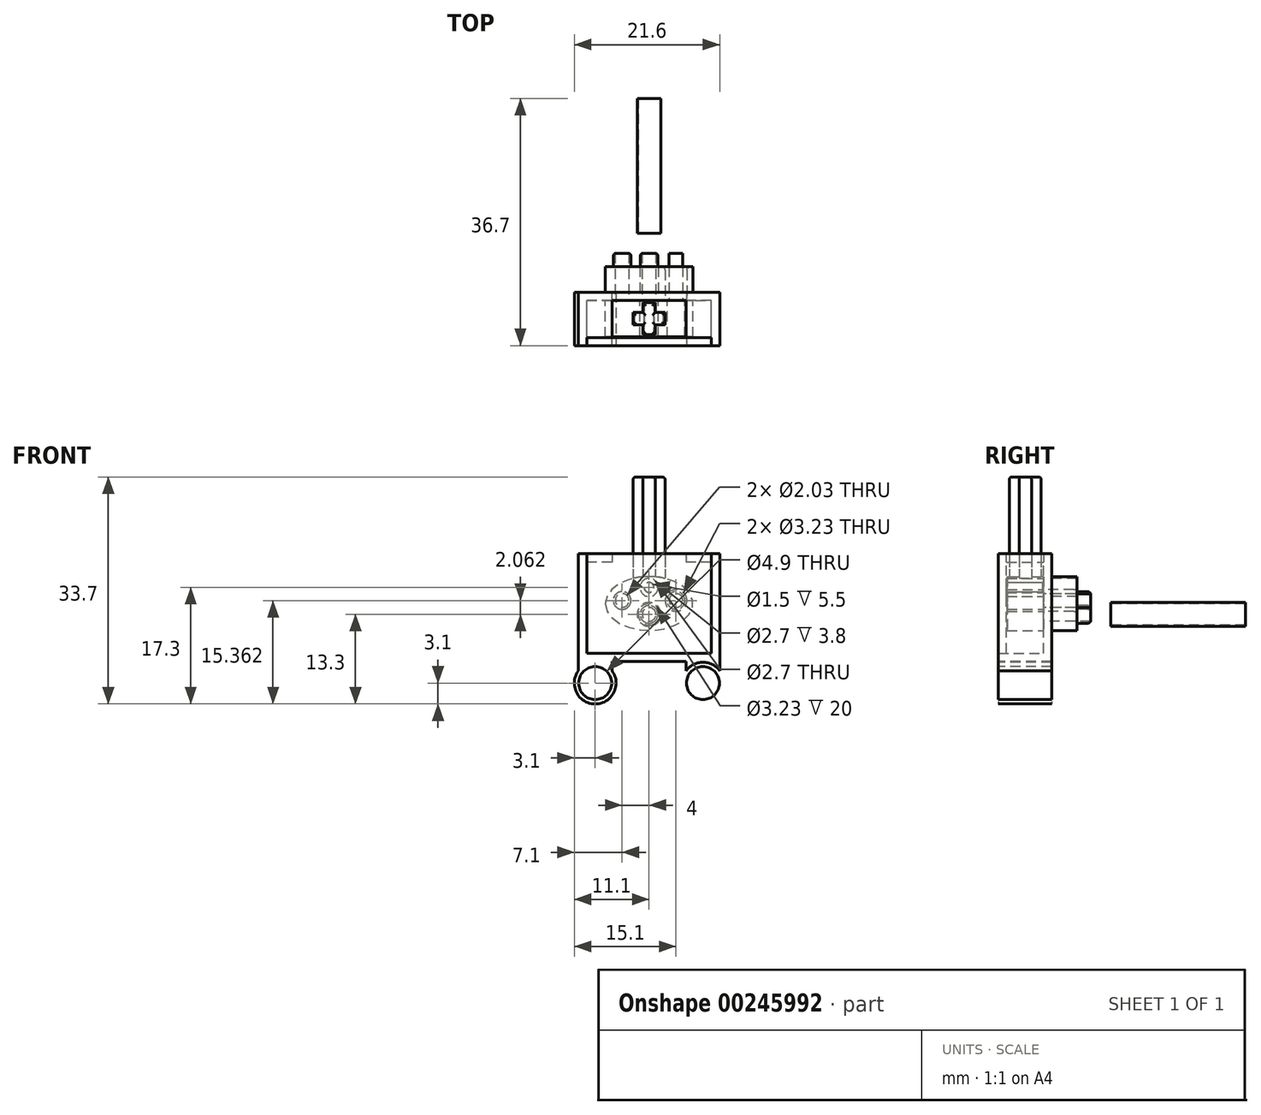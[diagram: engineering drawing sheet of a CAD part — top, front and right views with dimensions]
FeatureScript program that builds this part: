
annotation { "Feature Type Name" : "Feature", "Feature Type Description" : "" }
export const myFeature = defineFeature(function(context is Context, id is Id, definition is map)
    precondition{}
    {
        {
            var Q0;
            Q0=qCreatedBy(makeId("Front.planeOp"),FACE);
            var sketch = newSketch(context, id + "F0", { "sketchPlane" : qUnion([Q0])});
            skLineSegment(sketch, "E0", {"start": v(0, 5) * mm, "end": v(-10.5, 5) * mm});
            skLineSegment(sketch, "E1", {"start": v(-10.5, 5) * mm, "end": v(-10.5, -11) * mm});
            skLineSegment(sketch, "E2", {"start": v(-10.5, -11) * mm, "end": v(10.5, -11) * mm});
            skLineSegment(sketch, "E3", {"start": v(10.5, -11) * mm, "end": v(10.5, 5) * mm});
            skLineSegment(sketch, "E4", {"start": v(10.5, 5) * mm, "end": v(0, 5) * mm});
            skLineSegment(sketch, "E5", {"start": v(0, 5) * mm, "end": v(0, 0) * mm, "construction": true});
            skLineSegment(sketch, "E6.0", {"start": v(-9.25, 3.75) * mm, "end": v(-9.25, -9.75) * mm});
            skLineSegment(sketch, "E6.1", {"start": v(0, 3.75) * mm, "end": v(-9.25, 3.75) * mm});
            skLineSegment(sketch, "E6.2", {"start": v(-9.25, -9.75) * mm, "end": v(9.25, -9.75) * mm});
            skLineSegment(sketch, "E6.3", {"start": v(9.25, -9.75) * mm, "end": v(9.25, 3.75) * mm});
            skLineSegment(sketch, "E6.4", {"start": v(9.25, 3.75) * mm, "end": v(0, 3.75) * mm});
            skLineSegment(sketch, "E7", {"start": v(-5.5, 5) * mm, "end": v(-5.5, 3.75) * mm});
            skLineSegment(sketch, "E8.MirrorCS", {"start": v(5.5, 5) * mm, "end": v(5.5, 3.75) * mm});
            skLineSegment(sketch, "E9", {"start": v(0, -14.2) * mm, "end": v(-8, -14.2) * mm, "construction": true});
            skCircle(sketch, "E10", {"center": v(-8, -14.2) * mm, "radius": 2.45 * mm});
            skCircle(sketch, "E11.0", {"center": v(-8, -14.2) * mm, "radius": 3.1 * mm});
            skLineSegment(sketch, "E12.MirrorCS", {"start": v(0, -14.2) * mm, "end": v(8, -14.2) * mm, "construction": true});
            skCircle(sketch, "E13.MirrorC", {"center": v(8, -14.2) * mm, "radius": 2.45 * mm});
            skCircle(sketch, "E14.MirrorC", {"center": v(8, -14.2) * mm, "radius": 3.1 * mm});
            skLineSegment(sketch, "E15", {"start": v(-10.5, -11) * mm, "end": v(-10.5, -12.37) * mm});
            skLineSegment(sketch, "E16", {"start": v(-5.5, -11) * mm, "end": v(-5.5, -12.37) * mm});
            skLineSegment(sketch, "E17.MirrorCS", {"start": v(10.5, -11) * mm, "end": v(10.5, -12.37) * mm});
            skLineSegment(sketch, "E18.MirrorCS", {"start": v(5.5, -11) * mm, "end": v(5.5, -12.37) * mm});
            skLineSegment(sketch, "E19", {"start": v(-9.25, 3.75) * mm, "end": v(-9.25, 5) * mm});
            skLineSegment(sketch, "E20", {"start": v(9.25, 3.75) * mm, "end": v(9.25, 5) * mm});
            skCircle(sketch, "E21", {"center": v(0, 0) * mm, "radius": 0.75 * mm});
            skCircle(sketch, "E22.0", {"center": v(0, 0) * mm, "radius": 1.35 * mm});
            skCircle(sketch, "E23", {"center": v(0, -4) * mm, "radius": 1.62 * mm});
            skCircle(sketch, "E24", {"center": v(-4, -1.94) * mm, "radius": 1.62 * mm});
            skCircle(sketch, "E25.0", {"center": v(-4, -1.94) * mm, "radius": 1.02 * mm});
            skCircle(sketch, "E26.0", {"center": v(0, -4) * mm, "radius": 1.02 * mm});
            skCircle(sketch, "E27.MirrorC", {"center": v(4, -1.94) * mm, "radius": 1.62 * mm});
            skCircle(sketch, "E28.MirrorC", {"center": v(4, -1.94) * mm, "radius": 1.02 * mm});
            skCircle(sketch, "E29.0", {"center": v(0, -4) * mm, "radius": 1.32 * mm});
            skCircle(sketch, "E30.0", {"center": v(-4, -1.94) * mm, "radius": 1.32 * mm});
            skCircle(sketch, "E31.MirrorC", {"center": v(4, -1.94) * mm, "radius": 1.32 * mm});
            skLineSegment(sketch, "E32", {"start": v(0, 0) * mm, "end": v(0, -14.2) * mm, "construction": true});
            skEllipse(sketch, "E33", {"center": v(0, -2.39) * mm, "majorRadius": 6.5 * mm, "minorRadius": 4 * mm, "majorAxis": v(-1, 0)});
            skSolve(sketch);
        }
        {
            var Q0;
            {var subQ1=sQuery(id+"F0.wireOp",EDGE,"E6.0");Q0=makeQuery(id+"F0.imprint","IMPRINT",FACE,{"disambiguationData":[TD([[makeQuery(id+"F0.imprint","IMPRINT",EDGE,{"derivedFrom":subQ1}),1.0]])]});}
            var Q1;
            {var subQ8=sQuery(id+"F0.wireOp",EDGE,"E1");Q1=makeQuery(id+"F0.imprint","IMPRINT",FACE,{"disambiguationData":[TD([[makeQuery(id+"F0.imprint","IMPRINT",EDGE,{"derivedFrom":subQ8}),1.0]])]});}
            var Q2;
            {var subQ7=sQuery(id+"F0.wireOp",EDGE,"E7");Q2=makeQuery(id+"F0.imprint","IMPRINT",FACE,{"disambiguationData":[TD([[makeQuery(id+"F0.imprint","IMPRINT",EDGE,{"derivedFrom":subQ7}),1.0]])]});}
            var Q3;
            Q3=makeQuery(id+"F0.imprint","IMPRINT",FACE,{"disambiguationData":[TD([[makeQuery(id+"F0.imprint","IMPRINT",EDGE,{"derivedFrom":sQuery(id+"F0.wireOp",EDGE,"E10")}),-1.0]])]});
            var Q4;
            {var subQ0=sQuery(id+"F0.wireOp",EDGE,"E15");Q4=makeQuery(id+"F0.imprint","IMPRINT",FACE,{"disambiguationData":[TD([[makeQuery(id+"F0.imprint","IMPRINT",EDGE,{"derivedFrom":subQ0}),1.0]])]});}
            var Q5;
            Q5=makeQuery(id+"F0.imprint","IMPRINT",FACE,{"disambiguationData":[TD([[makeQuery(id+"F0.imprint","IMPRINT",EDGE,{"derivedFrom":sQuery(id+"F0.wireOp",EDGE,"E13.MirrorC")}),1.0]])]});
            var Q6;
            {var subQ0=sQuery(id+"F0.wireOp",EDGE,"E17.MirrorCS");Q6=makeQuery(id+"F0.imprint","IMPRINT",FACE,{"disambiguationData":[TD([[makeQuery(id+"F0.imprint","IMPRINT",EDGE,{"derivedFrom":subQ0}),-1.0]])]});}
            var Q7;
            {var subQ0=sQuery(id+"F0.wireOp",EDGE,"E7");Q7=makeQuery(id+"F0.imprint","IMPRINT",FACE,{"disambiguationData":[TD([[makeQuery(id+"F0.imprint","IMPRINT",EDGE,{"derivedFrom":subQ0}),-1.0]])]});}
            var Q8;
            {var subQ0=sQuery(id+"F0.wireOp",EDGE,"E8.MirrorCS");Q8=makeQuery(id+"F0.imprint","IMPRINT",FACE,{"disambiguationData":[TD([[makeQuery(id+"F0.imprint","IMPRINT",EDGE,{"derivedFrom":subQ0}),1.0]])]});}
            var Q9;
            Q9=makeQuery(id+"F0.imprint","IMPRINT",FACE,{"disambiguationData":[TD([[makeQuery(id+"F0.imprint","IMPRINT",EDGE,{"derivedFrom":sQuery(id+"F0.wireOp",EDGE,"E21")}),1.0]])]});
            var Q10;
            Q10=makeQuery(id+"F0.imprint","IMPRINT",FACE,{"disambiguationData":[TD([[makeQuery(id+"F0.imprint","IMPRINT",EDGE,{"derivedFrom":sQuery(id+"F0.wireOp",EDGE,"E21")}),-1.0]])]});
            var Q11;
            Q11=makeQuery(id+"F0.imprint","IMPRINT",FACE,{"disambiguationData":[TD([[makeQuery(id+"F0.imprint","IMPRINT",EDGE,{"derivedFrom":sQuery(id+"F0.wireOp",EDGE,"E24")}),1.0]])]});
            var Q12;
            Q12=makeQuery(id+"F0.imprint","IMPRINT",FACE,{"disambiguationData":[TD([[makeQuery(id+"F0.imprint","IMPRINT",EDGE,{"derivedFrom":sQuery(id+"F0.wireOp",EDGE,"E23")}),1.0]])]});
            var Q13;
            Q13=makeQuery(id+"F0.imprint","IMPRINT",FACE,{"disambiguationData":[TD([[makeQuery(id+"F0.imprint","IMPRINT",EDGE,{"derivedFrom":sQuery(id+"F0.wireOp",EDGE,"E27.MirrorC")}),-1.0]])]});
            var Q14;
            Q14=makeQuery(id+"F0.imprint","IMPRINT",FACE,{"disambiguationData":[TD([[makeQuery(id+"F0.imprint","IMPRINT",EDGE,{"derivedFrom":sQuery(id+"F0.wireOp",EDGE,"E22.0")}),-1.0]])]});
            var Q15;
            Q15=makeQuery(id+"F0.imprint","IMPRINT",FACE,{"disambiguationData":[TD([[makeQuery(id+"F0.imprint","IMPRINT",EDGE,{"derivedFrom":sQuery(id+"F0.wireOp",EDGE,"E28.MirrorC")}),1.0]])]});
            var Q16;
            Q16=makeQuery(id+"F0.imprint","IMPRINT",FACE,{"disambiguationData":[TD([[makeQuery(id+"F0.imprint","IMPRINT",EDGE,{"derivedFrom":sQuery(id+"F0.wireOp",EDGE,"E26.0")}),-1.0]])]});
            var Q17;
            Q17=makeQuery(id+"F0.imprint","IMPRINT",FACE,{"disambiguationData":[TD([[makeQuery(id+"F0.imprint","IMPRINT",EDGE,{"derivedFrom":sQuery(id+"F0.wireOp",EDGE,"E25.0")}),-1.0]])]});
            extrude(context, id + "F1", {"entities" : qUnion([Q0, Q1, Q2, Q3, Q4, Q5, Q6, Q7, Q8, Q9, Q10, Q11, Q12, Q13, Q14, Q15, Q16, Q17]), "oppositeDirection" : true, "depth" : 1.2 * mm, "offsetDistance" : 25 * mm});
        }
        {
            var Q0;
            {var subQ6=sQuery(id+"F0.wireOp",EDGE,"E1");Q0=makeQuery(id+"F0.imprint","IMPRINT",FACE,{"disambiguationData":[TD([[makeQuery(id+"F0.imprint","IMPRINT",EDGE,{"derivedFrom":subQ6}),1.0]])]});}
            var Q1;
            Q1=makeQuery(id+"F0.imprint","IMPRINT",FACE,{"disambiguationData":[TD([[makeQuery(id+"F0.imprint","IMPRINT",EDGE,{"derivedFrom":sQuery(id+"F0.wireOp",EDGE,"E10")}),-1.0]])]});
            var Q2;
            {var subQ0=sQuery(id+"F0.wireOp",EDGE,"E15");Q2=makeQuery(id+"F0.imprint","IMPRINT",FACE,{"disambiguationData":[TD([[makeQuery(id+"F0.imprint","IMPRINT",EDGE,{"derivedFrom":subQ0}),1.0]])]});}
            var Q3;
            Q3=makeQuery(id+"F0.imprint","IMPRINT",FACE,{"disambiguationData":[TD([[makeQuery(id+"F0.imprint","IMPRINT",EDGE,{"derivedFrom":sQuery(id+"F0.wireOp",EDGE,"E13.MirrorC")}),1.0]])]});
            var Q4;
            {var subQ0=sQuery(id+"F0.wireOp",EDGE,"E17.MirrorCS");Q4=makeQuery(id+"F0.imprint","IMPRINT",FACE,{"disambiguationData":[TD([[makeQuery(id+"F0.imprint","IMPRINT",EDGE,{"derivedFrom":subQ0}),-1.0]])]});}
            extrude(context, id + "F2", {"entities" : qUnion([Q0, Q1, Q2, Q3, Q4]), "operationType" : NewBodyOperationType.ADD, "depth" : (7.9 - 1.2) * mm, "offsetDistance" : 25 * mm});
        }
        {
            var Q0;
            {var subQ0=sQuery(id+"F0.wireOp",EDGE,"E7");Q0=makeQuery(id+"F0.imprint","IMPRINT",FACE,{"disambiguationData":[TD([[makeQuery(id+"F0.imprint","IMPRINT",EDGE,{"derivedFrom":subQ0}),-1.0]])]});}
            var Q1;
            {var subQ0=sQuery(id+"F0.wireOp",EDGE,"E8.MirrorCS");Q1=makeQuery(id+"F0.imprint","IMPRINT",FACE,{"disambiguationData":[TD([[makeQuery(id+"F0.imprint","IMPRINT",EDGE,{"derivedFrom":subQ0}),1.0]])]});}
            var Q2;
            Q2=makeQuery(id+"F0.imprint","IMPRINT",FACE,{"disambiguationData":[TD([[makeQuery(id+"F0.imprint","IMPRINT",EDGE,{"derivedFrom":sQuery(id+"F0.wireOp",EDGE,"E21")}),-1.0]])]});
            extrude(context, id + "F3", {"entities" : qUnion([Q0, Q1, Q2]), "operationType" : NewBodyOperationType.ADD, "depth" : (7.9 - 2.4) * mm, "offsetDistance" : 25 * mm});
        }
        {
            var Q0;
            Q0=makeQuery(id+"F0.imprint","IMPRINT",FACE,{"disambiguationData":[TD([[makeQuery(id+"F0.imprint","IMPRINT",EDGE,{"derivedFrom":sQuery(id+"F0.wireOp",EDGE,"E24")}),1.0]])]});
            var Q1;
            Q1=makeQuery(id+"F0.imprint","IMPRINT",FACE,{"disambiguationData":[TD([[makeQuery(id+"F0.imprint","IMPRINT",EDGE,{"derivedFrom":sQuery(id+"F0.wireOp",EDGE,"E23")}),1.0]])]});
            var Q2;
            Q2=makeQuery(id+"F0.imprint","IMPRINT",FACE,{"disambiguationData":[TD([[makeQuery(id+"F0.imprint","IMPRINT",EDGE,{"derivedFrom":sQuery(id+"F0.wireOp",EDGE,"E27.MirrorC")}),-1.0]])]});
            extrude(context, id + "F4", {"entities" : qUnion([Q0, Q1, Q2]), "operationType" : NewBodyOperationType.ADD, "oppositeDirection" : true, "depth" : 5 * mm, "offsetDistance" : 25 * mm});
        }
        {
            var Q0;
            Q0=makeQuery(id+"F0.imprint","IMPRINT",FACE,{"disambiguationData":[TD([[makeQuery(id+"F0.imprint","IMPRINT",EDGE,{"derivedFrom":sQuery(id+"F0.wireOp",EDGE,"E25.0")}),-1.0]])]});
            var Q1;
            Q1=makeQuery(id+"F0.imprint","IMPRINT",FACE,{"disambiguationData":[TD([[makeQuery(id+"F0.imprint","IMPRINT",EDGE,{"derivedFrom":sQuery(id+"F0.wireOp",EDGE,"E26.0")}),-1.0]])]});
            var Q2;
            Q2=makeQuery(id+"F0.imprint","IMPRINT",FACE,{"disambiguationData":[TD([[makeQuery(id+"F0.imprint","IMPRINT",EDGE,{"derivedFrom":sQuery(id+"F0.wireOp",EDGE,"E28.MirrorC")}),1.0]])]});
            extrude(context, id + "F5", {"entities" : qUnion([Q0, Q1, Q2]), "operationType" : NewBodyOperationType.ADD, "oppositeDirection" : true, "depth" : 7 * mm, "offsetDistance" : 25 * mm});
        }
        {
            var Q0;
            Q0=makeQuery(id+"F4.opExtrude","CAP_EDGE",EDGE,{"disambiguationData":[OSD([sQuery(id+"F0.wireOp",EDGE,"E27.MirrorC")])],"isStart":false});
            var Q1;
            Q1=makeQuery(id+"F4.opExtrude","CAP_EDGE",EDGE,{"disambiguationData":[OSD([sQuery(id+"F0.wireOp",EDGE,"E23")])],"isStart":false});
            var Q2;
            Q2=makeQuery(id+"F4.opExtrude","CAP_EDGE",EDGE,{"disambiguationData":[OSD([sQuery(id+"F0.wireOp",EDGE,"E24")])],"isStart":false});
            fillet(context, id + "F6", {"entities" : qUnion([Q0, Q1, Q2]), "radius" : 0.5 * mm, "tangentPropagation" : true, "allowEdgeOverflow" : false});
        }
        {
            var Q0;
            Q0=makeQuery(id+"F5.opExtrude","CAP_EDGE",EDGE,{"disambiguationData":[OSD([sQuery(id+"F0.wireOp",EDGE,"E31.MirrorC")])],"isStart":false});
            var Q1;
            Q1=makeQuery(id+"F5.opExtrude","CAP_EDGE",EDGE,{"disambiguationData":[OSD([sQuery(id+"F0.wireOp",EDGE,"E29.0")])],"isStart":false});
            var Q2;
            Q2=makeQuery(id+"F5.opExtrude","CAP_EDGE",EDGE,{"disambiguationData":[OSD([sQuery(id+"F0.wireOp",EDGE,"E30.0")])],"isStart":false});
            fillet(context, id + "F7", {"entities" : qUnion([Q0, Q1, Q2]), "radius" : 0.5 * mm, "tangentPropagation" : true, "allowEdgeOverflow" : false});
        }
        {
            var Q0;
            Q0=makeQuery(id+"F3.opExtrude","CAP_FACE",FACE,{"disambiguationData":[OSD([sQuery(id+"F0.wireOp",EDGE,"E0"),sQuery(id+"F0.wireOp",EDGE,"E6.1"),sQuery(id+"F0.wireOp",EDGE,"E7"),sQuery(id+"F0.wireOp",EDGE,"E19")])],"isStart":false});
            var sketch = newSketch(context, id + "F8", { "sketchPlane" : qUnion([Q0])});
            skLineSegment(sketch, "E34.0", {"start": v(-9.25, 5) * mm, "end": v(-9.25, -9.75) * mm});
            skLineSegment(sketch, "E35.0", {"start": v(-9.25, -9.75) * mm, "end": v(9.25, -9.75) * mm});
            skLineSegment(sketch, "E36.0", {"start": v(9.25, -9.75) * mm, "end": v(9.25, 5) * mm});
            skLineSegment(sketch, "E37.0", {"start": v(5.5, 5) * mm, "end": v(-5.5, 5) * mm});
            skLineSegment(sketch, "E38.0", {"start": v(-5.5, 5) * mm, "end": v(-9.25, 5) * mm});
            skLineSegment(sketch, "E39.0", {"start": v(9.25, 5) * mm, "end": v(5.5, 5) * mm});
            skCircle(sketch, "E40.0", {"center": v(0, 0) * mm, "radius": 0.72 * mm});
            skSolve(sketch);
        }
        {
            var Q0;
            Q0 = qSketchRegion(id + "F8", true);
            var Q1;
            Q1=makeQuery(id+"F8.imprint","IMPRINT",FACE,{"disambiguationData":[TD([[makeQuery(id+"F8.imprint","IMPRINT",EDGE,{"derivedFrom":sQuery(id+"F8.wireOp",EDGE,"E40.0")}),1.0]])]});
            extrude(context, id + "F9", {"entities" : qUnion([Q0, Q1]), "depth" : 1.2 * mm, "offsetDistance" : 25 * mm});
        }
        {
            var Q0;
            Q0=makeQuery(id+"F8.imprint","IMPRINT",FACE,{"disambiguationData":[TD([[makeQuery(id+"F8.imprint","IMPRINT",EDGE,{"derivedFrom":sQuery(id+"F8.wireOp",EDGE,"E40.0")}),1.0]])]});
            extrude(context, id + "F10", {"entities" : qUnion([Q0]), "operationType" : NewBodyOperationType.ADD, "oppositeDirection" : true, "depth" : 5.4 * mm, "offsetDistance" : 25 * mm});
        }
        {
            var Q0;
            Q0=makeQuery(id+"F0.imprint","IMPRINT",FACE,{"disambiguationData":[TD([[makeQuery(id+"F0.imprint","IMPRINT",EDGE,{"derivedFrom":sQuery(id+"F0.wireOp",EDGE,"E22.0")}),-1.0]])]});
            var Q1;
            Q1=makeQuery(id+"F0.imprint","IMPRINT",FACE,{"disambiguationData":[TD([[makeQuery(id+"F0.imprint","IMPRINT",EDGE,{"derivedFrom":sQuery(id+"F0.wireOp",EDGE,"E24")}),1.0]])]});
            var Q2;
            Q2=makeQuery(id+"F0.imprint","IMPRINT",FACE,{"disambiguationData":[TD([[makeQuery(id+"F0.imprint","IMPRINT",EDGE,{"derivedFrom":sQuery(id+"F0.wireOp",EDGE,"E25.0")}),-1.0]])]});
            var Q3;
            Q3=makeQuery(id+"F0.imprint","IMPRINT",FACE,{"disambiguationData":[TD([[makeQuery(id+"F0.imprint","IMPRINT",EDGE,{"derivedFrom":sQuery(id+"F0.wireOp",EDGE,"E25.0")}),1.0]])]});
            var Q4;
            Q4=makeQuery(id+"F0.imprint","IMPRINT",FACE,{"disambiguationData":[TD([[makeQuery(id+"F0.imprint","IMPRINT",EDGE,{"derivedFrom":sQuery(id+"F0.wireOp",EDGE,"E23")}),1.0]])]});
            var Q5;
            Q5=makeQuery(id+"F0.imprint","IMPRINT",FACE,{"disambiguationData":[TD([[makeQuery(id+"F0.imprint","IMPRINT",EDGE,{"derivedFrom":sQuery(id+"F0.wireOp",EDGE,"E26.0")}),-1.0]])]});
            var Q6;
            Q6=makeQuery(id+"F0.imprint","IMPRINT",FACE,{"disambiguationData":[TD([[makeQuery(id+"F0.imprint","IMPRINT",EDGE,{"derivedFrom":sQuery(id+"F0.wireOp",EDGE,"E26.0")}),1.0]])]});
            var Q7;
            Q7=makeQuery(id+"F0.imprint","IMPRINT",FACE,{"disambiguationData":[TD([[makeQuery(id+"F0.imprint","IMPRINT",EDGE,{"derivedFrom":sQuery(id+"F0.wireOp",EDGE,"E27.MirrorC")}),-1.0]])]});
            var Q8;
            Q8=makeQuery(id+"F0.imprint","IMPRINT",FACE,{"disambiguationData":[TD([[makeQuery(id+"F0.imprint","IMPRINT",EDGE,{"derivedFrom":sQuery(id+"F0.wireOp",EDGE,"E28.MirrorC")}),1.0]])]});
            var Q9;
            Q9=makeQuery(id+"F0.imprint","IMPRINT",FACE,{"disambiguationData":[TD([[makeQuery(id+"F0.imprint","IMPRINT",EDGE,{"derivedFrom":sQuery(id+"F0.wireOp",EDGE,"E28.MirrorC")}),-1.0]])]});
            extrude(context, id + "F11", {"entities" : qUnion([Q0, Q1, Q2, Q3, Q4, Q5, Q6, Q7, Q8, Q9]), "depth" : 5.4 * mm, "offsetDistance" : 25 * mm});
        }
        {
            var Q0;
            Q0=qCreatedBy(makeId("Top.planeOp"),FACE);
            cPlane(context, id + "F12", {"entities" : qUnion([Q0]), "cplaneType" : CPlaneType.OFFSET, "offset" : 1.4 * mm, "width" : 150 * mm, "height" : 150 * mm});
        }
        {
            var Q0;
            Q0=qCreatedBy(id+"F12.planeOp",FACE);
            var sketch = newSketch(context, id + "F13", { "sketchPlane" : qUnion([Q0])});
            skLineSegment(sketch, "E41.0", {"start": v(6.5, -5.4) * mm, "end": v(-6.5, -5.4) * mm, "construction": true});
            skLineSegment(sketch, "E42.0", {"start": v(6.5, 0) * mm, "end": v(-6.5, 0) * mm, "construction": true});
            skLineSegment(sketch, "E43", {"start": v(-6.5, 0) * mm, "end": v(-6.5, -5.4) * mm, "construction": true});
            skLineSegment(sketch, "E44", {"start": v(6.5, 0) * mm, "end": v(6.5, -5.4) * mm, "construction": true});
            skLineSegment(sketch, "E45", {"start": v(-6.5, -2.7) * mm, "end": v(6.5, -2.7) * mm, "construction": true});
            skLineSegment(sketch, "E46", {"start": v(0, 0) * mm, "end": v(0, -2.7) * mm, "construction": true});
            skLineSegment(sketch, "E47", {"start": v(0, -2.7) * mm, "end": v(0, -5.4) * mm, "construction": true});
            skLineSegment(sketch, "E48", {"start": v(0, -0.33) * mm, "end": v(-0.92, -0.33) * mm});
            skLineSegment(sketch, "E49", {"start": v(-0.92, -0.33) * mm, "end": v(-0.92, -1.78) * mm});
            skLineSegment(sketch, "E50", {"start": v(-0.92, -1.78) * mm, "end": v(-2.38, -1.78) * mm});
            skLineSegment(sketch, "E51", {"start": v(-2.38, -1.78) * mm, "end": v(-2.38, -2.7) * mm});
            skLineSegment(sketch, "E52.MirrorCS", {"start": v(2.38, -1.78) * mm, "end": v(2.38, -2.7) * mm});
            skLineSegment(sketch, "E53.MirrorCS", {"start": v(0.92, -1.78) * mm, "end": v(2.38, -1.78) * mm});
            skLineSegment(sketch, "E54.MirrorCS", {"start": v(0, -0.33) * mm, "end": v(0.92, -0.33) * mm});
            skLineSegment(sketch, "E55.MirrorCS", {"start": v(0.92, -0.33) * mm, "end": v(0.92, -1.78) * mm});
            skLineSegment(sketch, "E56.MirrorCS", {"start": v(0.92, -5.07) * mm, "end": v(0.92, -3.62) * mm});
            skLineSegment(sketch, "E57.MirrorCS", {"start": v(0.92, -3.62) * mm, "end": v(2.38, -3.62) * mm});
            skLineSegment(sketch, "E58.MirrorCS", {"start": v(2.38, -3.62) * mm, "end": v(2.38, -2.7) * mm});
            skLineSegment(sketch, "E59.MirrorCS", {"start": v(-2.38, -3.62) * mm, "end": v(-2.38, -2.7) * mm});
            skLineSegment(sketch, "E60.MirrorCS", {"start": v(-0.92, -3.62) * mm, "end": v(-2.38, -3.62) * mm});
            skLineSegment(sketch, "E61.MirrorCS", {"start": v(-0.92, -5.07) * mm, "end": v(-0.92, -3.62) * mm});
            skLineSegment(sketch, "E62.MirrorCS", {"start": v(0, -5.07) * mm, "end": v(-0.92, -5.07) * mm});
            skLineSegment(sketch, "E63.MirrorCS", {"start": v(0, -5.07) * mm, "end": v(0.92, -5.07) * mm});
            skLineSegment(sketch, "E64.0", {"start": v(0.75, 0) * mm, "end": v(-0.75, 0) * mm});
            skSolve(sketch);
        }
        {
            var Q0;
            Q0=makeQuery(id+"F13.imprint","IMPRINT",FACE,{"disambiguationData":[TD([[makeQuery(id+"F13.imprint","IMPRINT",EDGE,{"derivedFrom":sQuery(id+"F13.wireOp",EDGE,"E49")}),1.0]])]});
            extrude(context, id + "F14", {"entities" : qUnion([Q0]), "operationType" : NewBodyOperationType.ADD, "depth" : 15 * mm, "offsetDistance" : 25 * mm});
        }
        {
            var Q0;
            Q0=makeQuery(id+"F14.opExtrude","CAP_FACE",FACE,{"disambiguationData":[OSD([sQuery(id+"F13.wireOp",EDGE,"E49"),sQuery(id+"F13.wireOp",EDGE,"E50"),sQuery(id+"F13.wireOp",EDGE,"E51"),sQuery(id+"F13.wireOp",EDGE,"E52.MirrorCS"),sQuery(id+"F13.wireOp",EDGE,"E53.MirrorCS"),sQuery(id+"F13.wireOp",EDGE,"E55.MirrorCS"),sQuery(id+"F13.wireOp",EDGE,"E54.MirrorCS"),sQuery(id+"F13.wireOp",EDGE,"E48"),sQuery(id+"F13.wireOp",EDGE,"E56.MirrorCS"),sQuery(id+"F13.wireOp",EDGE,"E57.MirrorCS"),sQuery(id+"F13.wireOp",EDGE,"E58.MirrorCS"),sQuery(id+"F13.wireOp",EDGE,"E59.MirrorCS"),sQuery(id+"F13.wireOp",EDGE,"E60.MirrorCS"),sQuery(id+"F13.wireOp",EDGE,"E61.MirrorCS"),sQuery(id+"F13.wireOp",EDGE,"E62.MirrorCS"),sQuery(id+"F13.wireOp",EDGE,"E63.MirrorCS")])],"isStart":false});
            fillet(context, id + "F15", {"entities" : qUnion([Q0]), "radius" : 0.4 * mm, "tangentPropagation" : true, "allowEdgeOverflow" : false});
        }
        {
            var Q0;
            Q0=qCreatedBy(makeId("Front.planeOp"),FACE);
            cPlane(context, id + "F16", {"entities" : qUnion([Q0]), "cplaneType" : CPlaneType.OFFSET, "offset" : 10 * mm, "oppositeDirection" : true, "width" : 150 * mm, "height" : 150 * mm});
        }
        {
            var Q0;
            Q0=qCreatedBy(id+"F16.planeOp",FACE);
            var sketch = newSketch(context, id + "F17", { "sketchPlane" : qUnion([Q0])});
            skCircle(sketch, "E65.0", {"center": v(0, -4) * mm, "radius": 1.62 * mm});
            skCircle(sketch, "E66.0", {"center": v(0, -4) * mm, "radius": 1.77 * mm});
            skSolve(sketch);
        }
        {
            var Q0;
            Q0=makeQuery(id+"F17.imprint","IMPRINT",FACE,{"disambiguationData":[TD([[makeQuery(id+"F17.imprint","IMPRINT",EDGE,{"derivedFrom":sQuery(id+"F17.wireOp",EDGE,"E65.0")}),-1.0]])]});
            var Q1;
            Q1=sQuery(id+"F17.wireOp",EDGE,"E65.0");
            extrude(context, id + "F18", {"entities" : qUnion([Q0]), "surfaceEntities" : qUnion([Q1]), "oppositeDirection" : true, "depth" : 20 * mm, "offsetDistance" : 25 * mm});
        }
    });
